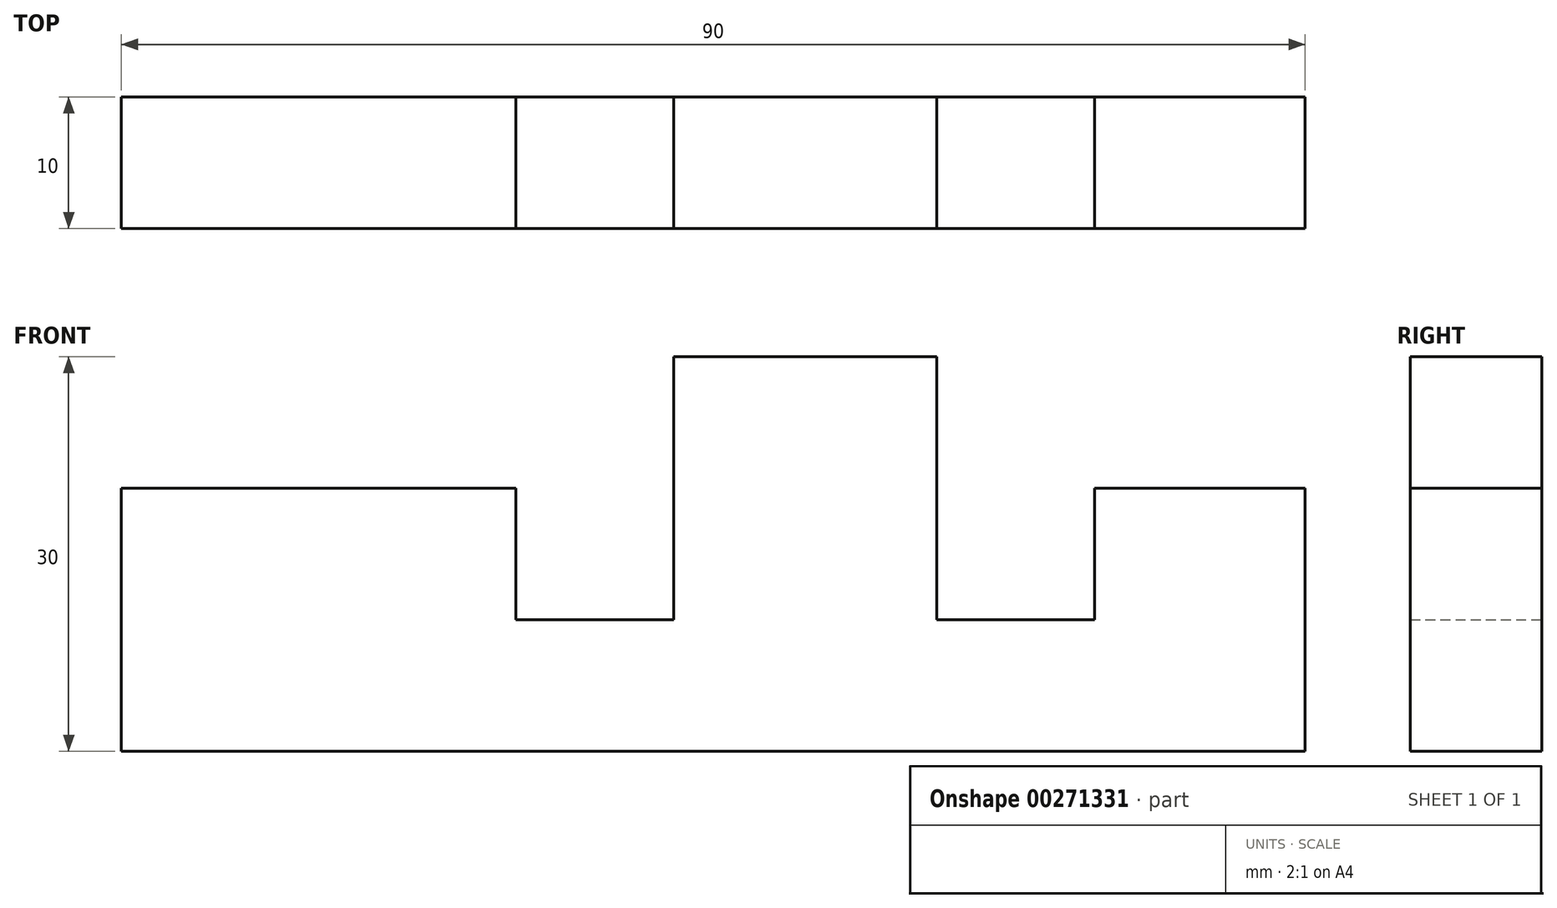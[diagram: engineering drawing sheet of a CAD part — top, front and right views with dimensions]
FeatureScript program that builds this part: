
annotation { "Feature Type Name" : "Feature", "Feature Type Description" : "" }
export const myFeature = defineFeature(function(context is Context, id is Id, definition is map)
    precondition{}
    {
        {
            var Q0;
            Q0=qCreatedBy(makeId("Front.planeOp"),FACE);
            var sketch = newSketch(context, id + "F0", { "sketchPlane" : qUnion([Q0])});
            skLineSegment(sketch, "E0", {"start": v(0, 0) * mm, "end": v(90, 0) * mm});
            skLineSegment(sketch, "E1", {"start": v(0, 0) * mm, "end": v(0, 20) * mm});
            skLineSegment(sketch, "E2", {"start": v(0, 20) * mm, "end": v(30, 20) * mm});
            skLineSegment(sketch, "E3", {"start": v(30, 20) * mm, "end": v(30, 10) * mm});
            skLineSegment(sketch, "E4", {"start": v(30, 10) * mm, "end": v(42, 10) * mm});
            skLineSegment(sketch, "E5", {"start": v(42, 10) * mm, "end": v(42, 30) * mm});
            skLineSegment(sketch, "E6", {"start": v(42, 30) * mm, "end": v(62, 30) * mm});
            skLineSegment(sketch, "E7", {"start": v(62, 30) * mm, "end": v(62, 10) * mm});
            skLineSegment(sketch, "E8", {"start": v(62, 10) * mm, "end": v(74, 10) * mm});
            skLineSegment(sketch, "E9", {"start": v(74, 10) * mm, "end": v(74, 20) * mm});
            skPoint(sketch, "E9.endSnap0", {"position": v(42, 20) * mm});
            skLineSegment(sketch, "E10", {"start": v(74, 20) * mm, "end": v(90, 20) * mm});
            skLineSegment(sketch, "E11", {"start": v(90, 20) * mm, "end": v(90, 0) * mm});
            skSolve(sketch);
        }
        {
            var Q0;
            Q0=makeQuery(id+"F0.imprint","IMPRINT",FACE,{"disambiguationData":[TD([[makeQuery(id+"F0.imprint","IMPRINT",EDGE,{"derivedFrom":sQuery(id+"F0.wireOp",EDGE,"E0")}),1.0]])]});
            extrude(context, id + "F1", {"entities" : qUnion([Q0]), "depth" : 10 * mm});
        }
    });
